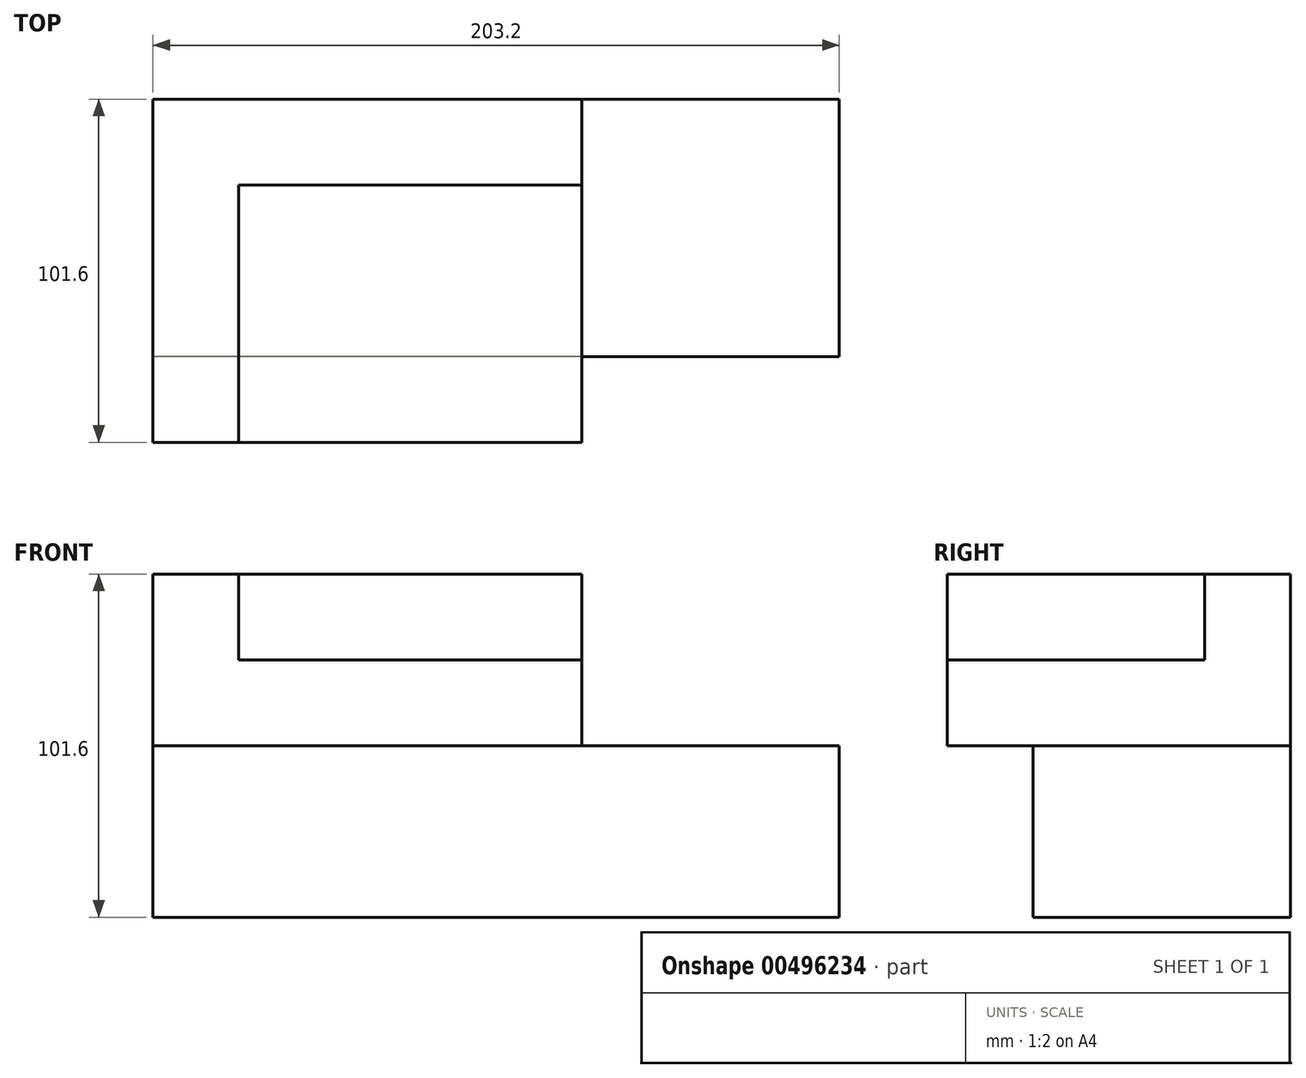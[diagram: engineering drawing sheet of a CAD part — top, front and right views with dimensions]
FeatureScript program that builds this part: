
annotation { "Feature Type Name" : "Feature", "Feature Type Description" : "" }
export const myFeature = defineFeature(function(context is Context, id is Id, definition is map)
    precondition{}
    {
        {
            var Q0;
            Q0=qCreatedBy(makeId("Front.planeOp"),FACE);
            var sketch = newSketch(context, id + "F0", { "sketchPlane" : qUnion([Q0])});
            skLineSegment(sketch, "E0.bottom", {"start": v(0, 0) * mm, "end": v(76.2, 0) * mm});
            skLineSegment(sketch, "E0.top", {"start": v(0, 50.8) * mm, "end": v(76.2, 50.8) * mm});
            skLineSegment(sketch, "E0.left", {"start": v(0, 0) * mm, "end": v(0, 50.8) * mm});
            skLineSegment(sketch, "E0.right", {"start": v(76.2, 0) * mm, "end": v(76.2, 50.8) * mm});
            skSolve(sketch);
        }
        {
            var Q0;
            Q0 = qSketchRegion(id + "F0", true);
            extrude(context, id + "F1", {"entities" : qUnion([Q0]), "depth" : 203.2 * mm});
        }
        {
            var Q0;
            Q0=makeQuery(id+"F1.opExtrude","CAP_FACE",FACE,{"disambiguationData":[OSD([sQuery(id+"F0.wireOp",EDGE,"E0.bottom"),sQuery(id+"F0.wireOp",EDGE,"E0.top"),sQuery(id+"F0.wireOp",EDGE,"E0.left"),sQuery(id+"F0.wireOp",EDGE,"E0.right")])],"isStart":true});
            var sketch = newSketch(context, id + "F2", { "sketchPlane" : qUnion([Q0])});
            skLineSegment(sketch, "E1.bottom", {"start": v(-76.2, 50.8) * mm, "end": v(25.4, 50.8) * mm});
            skLineSegment(sketch, "E1.top", {"start": v(-76.2, 101.6) * mm, "end": v(25.4, 101.6) * mm});
            skLineSegment(sketch, "E1.left", {"start": v(-76.2, 50.8) * mm, "end": v(-76.2, 101.6) * mm});
            skLineSegment(sketch, "E1.right", {"start": v(25.4, 50.8) * mm, "end": v(25.4, 101.6) * mm});
            skSolve(sketch);
        }
        {
            var Q0;
            Q0=makeQuery(id+"F2.imprint","IMPRINT",FACE,{"disambiguationData":[TD([[makeQuery(id+"F2.imprint","IMPRINT",EDGE,{"derivedFrom":sQuery(id+"F2.wireOp",EDGE,"E1.top")}),-1.0]])]});
            extrude(context, id + "F3", {"entities" : qUnion([Q0]), "operationType" : NewBodyOperationType.ADD, "oppositeDirection" : true, "depth" : 127 * mm});
        }
        {
            var Q0;
            Q0=makeQuery(id+"F3.opExtrude","CAP_FACE",FACE,{"disambiguationData":[OSD([sQuery(id+"F2.wireOp",EDGE,"E1.bottom"),sQuery(id+"F2.wireOp",EDGE,"E1.top"),sQuery(id+"F2.wireOp",EDGE,"E1.left"),sQuery(id+"F2.wireOp",EDGE,"E1.right")])],"isStart":false});
            var sketch = newSketch(context, id + "F4", { "sketchPlane" : qUnion([Q0])});
            skLineSegment(sketch, "E2.bottom", {"start": v(-25.4, 101.6) * mm, "end": v(50.8, 101.6) * mm});
            skLineSegment(sketch, "E2.top", {"start": v(-25.4, 76.2) * mm, "end": v(50.8, 76.2) * mm});
            skLineSegment(sketch, "E2.left", {"start": v(-25.4, 101.6) * mm, "end": v(-25.4, 76.2) * mm});
            skLineSegment(sketch, "E2.right", {"start": v(50.8, 101.6) * mm, "end": v(50.8, 76.2) * mm});
            skSolve(sketch);
        }
        {
            var Q0;
            Q0 = qSketchRegion(id + "F4", true);
            extrude(context, id + "F5", {"entities" : qUnion([Q0]), "operationType" : NewBodyOperationType.REMOVE, "oppositeDirection" : true, "depth" : 101.6 * mm});
        }
        {
            var Q0;
            Q0=makeQuery(id+"F1.opExtrude","SWEPT_BODY",BODY,{"disambiguationData":[OSD([sQuery(id+"F0.wireOp",EDGE,"E0.bottom"),sQuery(id+"F0.wireOp",EDGE,"E0.top"),sQuery(id+"F0.wireOp",EDGE,"E0.left"),sQuery(id+"F0.wireOp",EDGE,"E0.right")])]});
            var Q1;
            Q1=makeQuery(id+"F3.opExtrude","CAP_EDGE",EDGE,{"disambiguationData":[OSD([sQuery(id+"F2.wireOp",EDGE,"E1.left")])],"isStart":false});
            transform(context, id + "F6", {"entities" : qUnion([Q0]), "transformType" : TransformType.ROTATION, "transformAxis" : qUnion([Q1]), "angle" : 90 * degree, "makeCopy" : false});
        }
    });
